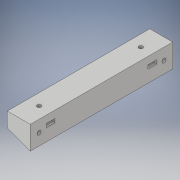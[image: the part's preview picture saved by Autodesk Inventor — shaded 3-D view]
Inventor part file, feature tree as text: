
AUTODESK INVENTOR PART (.ipt)
format: ipt  version: 2019 (Build 230136000, 136)  size: 138,240 bytes
history: native  units: mm
features: extrude x4, sketch x4, other x2, projected_geometry x2
ambient origin geometry x8: Origin, YZ Plane, XZ Plane, XY Plane, X Axis, Y Axis, Z Axis, Center Point
bodies: Body1 (feature_tree)
feature tree (12):
  other  "Твердое тело1"
  extrude  "Выдавливание1"  Depth=10.0mm
  extrude  "Выдавливание2"  Depth=15.8mm
  other  "РабПлоскость1"
  extrude  "Выдавливание3"  Depth=16.0mm
  extrude  "Выдавливание4"  Depth=98.0mm TaperAngle=0.0deg
  sketch  "Эскиз1"
  sketch  "Эскиз2"
  sketch  "Эскиз4"
  sketch  "Эскиз5"
  projected_geometry  "Спроецированная петля1"
  projected_geometry  "Спроецированная петля2"
